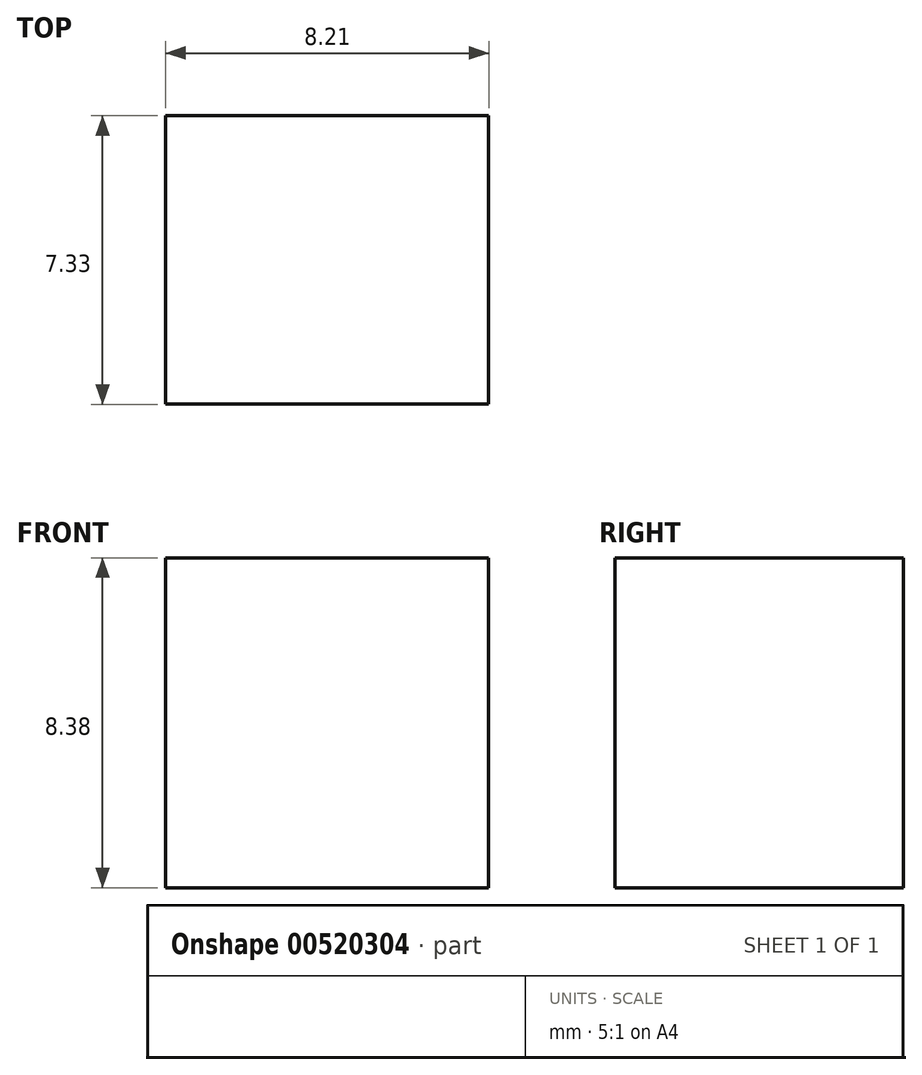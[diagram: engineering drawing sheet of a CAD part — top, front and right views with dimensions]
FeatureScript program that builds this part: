
annotation { "Feature Type Name" : "Feature", "Feature Type Description" : "" }
export const myFeature = defineFeature(function(context is Context, id is Id, definition is map)
    precondition{}
    {
        {
            var Q0;
            Q0=qCreatedBy(makeId("Top.planeOp"),FACE);
            var sketch = newSketch(context, id + "F0", { "sketchPlane" : qUnion([Q0])});
            skLineSegment(sketch, "E0.bottom", {"start": v(0, 0) * mm, "end": v(8.2, 0) * mm});
            skLineSegment(sketch, "E0.top", {"start": v(0, -7.33) * mm, "end": v(8.2, -7.33) * mm});
            skLineSegment(sketch, "E0.left", {"start": v(0, 0) * mm, "end": v(0, -7.33) * mm});
            skLineSegment(sketch, "E0.right", {"start": v(8.2, 0) * mm, "end": v(8.2, -7.33) * mm});
            skSolve(sketch);
        }
        {
            var Q0;
            Q0=makeQuery(id+"F0.imprint","IMPRINT",FACE,{"disambiguationData":[TD([[makeQuery(id+"F0.imprint","IMPRINT",EDGE,{"derivedFrom":sQuery(id+"F0.wireOp",EDGE,"E0.bottom")}),-1.0]])]});
            extrude(context, id + "F1", {"entities" : qUnion([Q0]), "depth" : 8.38 * mm, "offsetDistance" : 25.4 * mm});
        }
    });
